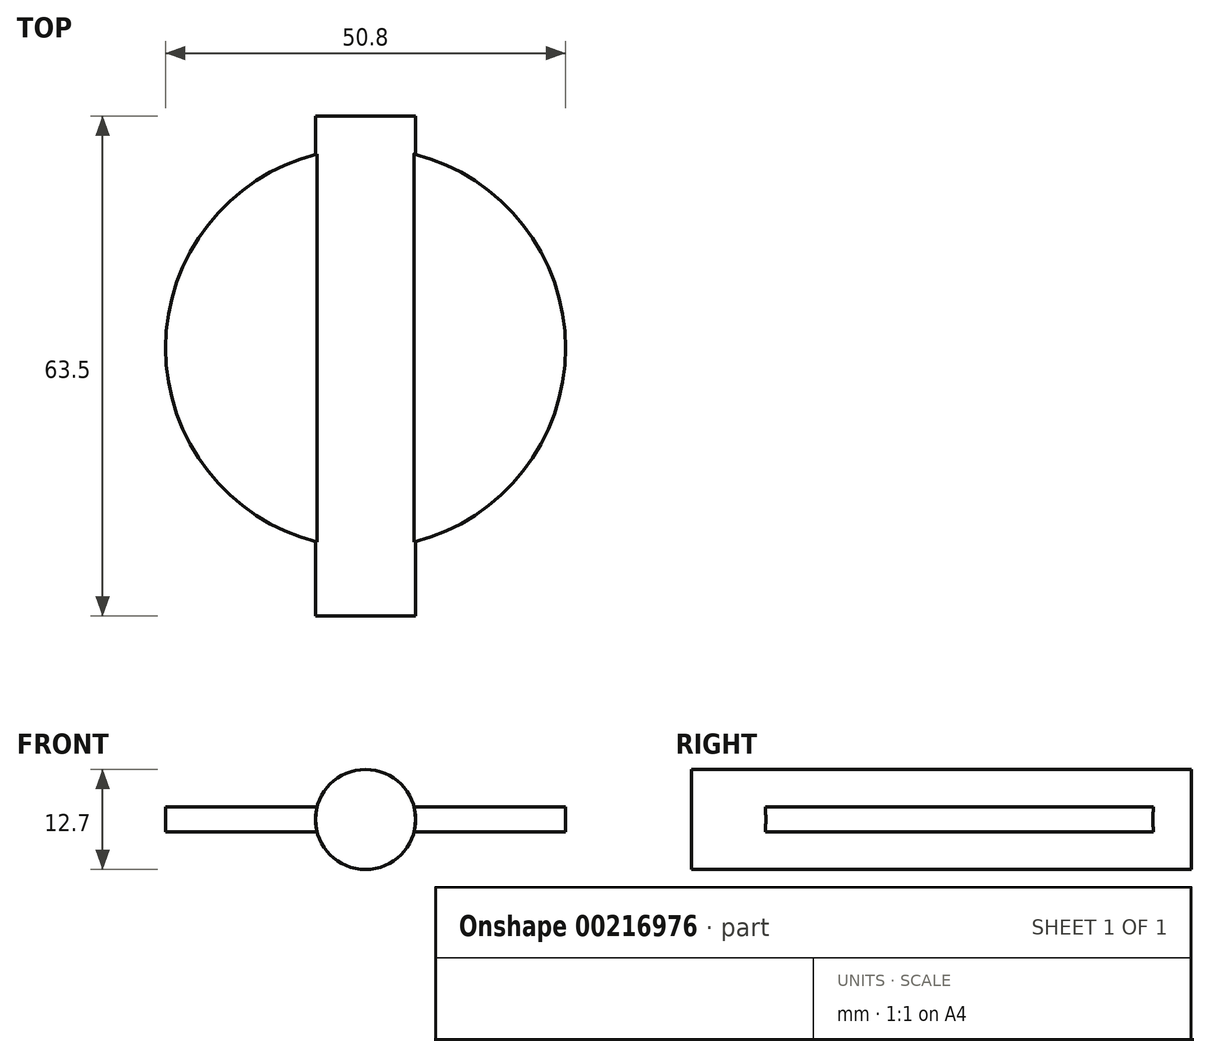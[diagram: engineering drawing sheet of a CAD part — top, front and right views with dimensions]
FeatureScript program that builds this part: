
annotation { "Feature Type Name" : "Feature", "Feature Type Description" : "" }
export const myFeature = defineFeature(function(context is Context, id is Id, definition is map)
    precondition{}
    {
        {
            var Q0;
            Q0=qCreatedBy(makeId("Front.planeOp"),FACE);
            var sketch = newSketch(context, id + "F0", { "sketchPlane" : qUnion([Q0])});
            skCircle(sketch, "E0", {"center": v(0, 0) * mm, "radius": 6.35 * mm});
            skSolve(sketch);
        }
        {
            var Q0;
            Q0 = qSketchRegion(id + "F0", true);
            extrude(context, id + "F1", {"entities" : qUnion([Q0]), "depth" : 63.5 * mm});
        }
        {
            var Q0;
            Q0=qCreatedBy(makeId("Top.planeOp"),FACE);
            var sketch = newSketch(context, id + "F2", { "sketchPlane" : qUnion([Q0])});
            skCircle(sketch, "E1", {"center": v(0, -29.47) * mm, "radius": 25.4 * mm});
            skSolve(sketch);
        }
        {
            var Q0;
            Q0=makeQuery(id+"F2.imprint","IMPRINT",FACE,{"disambiguationData":[TD([[makeQuery(id+"F2.imprint","IMPRINT",EDGE,{"derivedFrom":sQuery(id+"F2.wireOp",EDGE,"E1")}),1.0]])]});
            extrude(context, id + "F3", {"entities" : qUnion([Q0]), "operationType" : NewBodyOperationType.ADD, "depth" : 3.17 * mm, "symmetric" : true});
        }
    });
